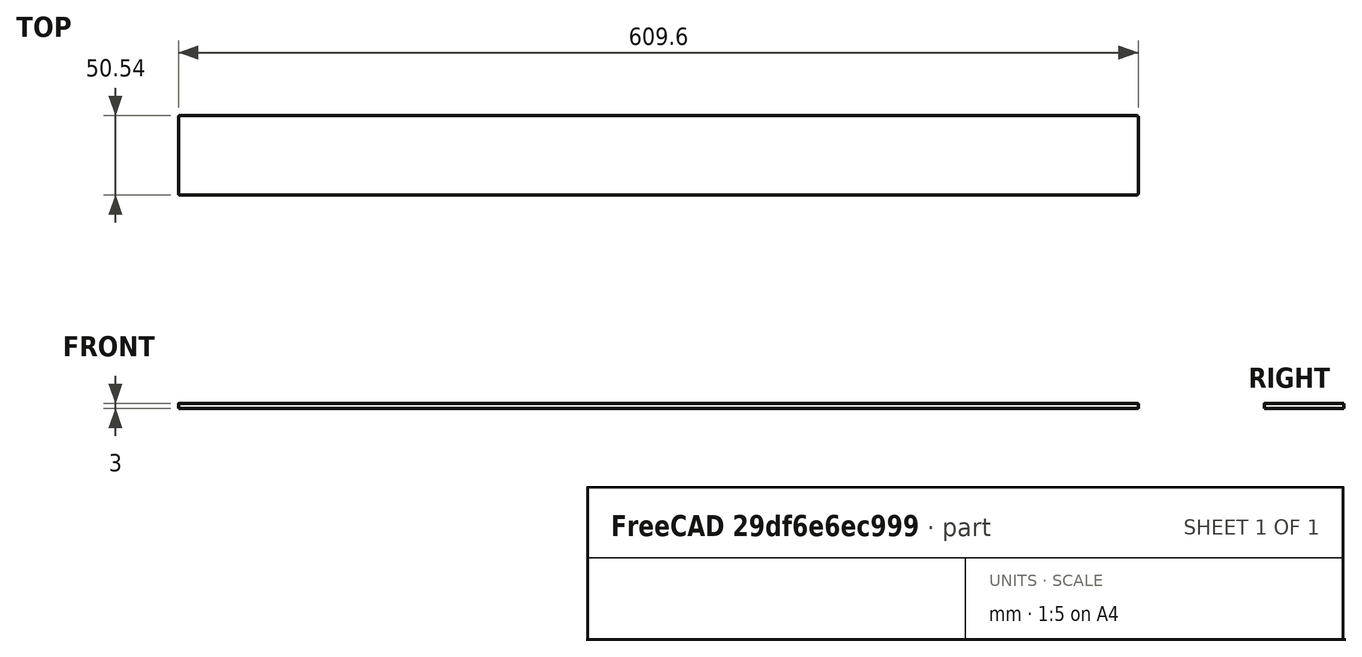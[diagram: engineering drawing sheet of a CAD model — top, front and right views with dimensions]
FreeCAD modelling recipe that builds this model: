
FCSTD DOCUMENT  (FreeCAD 0.20R29603 (Git))
Label: floor_24in
License: All rights reserved
LicenseURL: http://en.wikipedia.org/wiki/All_rights_reserved
objects: Sketcher::SketchObject×1, Spreadsheet::Sheet×1, PartDesign::Pad×1, PartDesign::Body×1
note: 4 computed .brp shape members not serialized (recipe doc carries the construction recipe); baked Part::Feature solids carry a one-line shape summary decoded from their .brp

FEATURE [Sketcher::SketchObject] Sketch
  FullyConstrained = true
  MapMode = 5
  Support = -> [XY_Plane]
  expr: Constraints[19] = Spreadsheet.FilletRadius
  expr: Constraints[20] = Spreadsheet.Width
  expr: Constraints[21] = Spreadsheet.Length
  sketch-geometry (10):
    g0: ArcOfCircle CenterX=-303.8 CenterY=24.275 CenterZ=0 NormalX=0 NormalY=0 NormalZ=1 AngleXU=0 Radius=1 StartAngle=1.5708 EndAngle=3.14159
    g1: LineSegment StartX=-303.8 StartY=25.275 StartZ=0 EndX=303.8 EndY=25.275 EndZ=0
    g2: ArcOfCircle CenterX=303.8 CenterY=24.275 CenterZ=0 NormalX=0 NormalY=0 NormalZ=1 AngleXU=0 Radius=1 StartAngle=1e-15 EndAngle=1.5708
    g3: LineSegment StartX=304.8 StartY=24.275 StartZ=0 EndX=304.8 EndY=-24.275 EndZ=0
    g4: ArcOfCircle CenterX=303.8 CenterY=-24.275 CenterZ=0 NormalX=0 NormalY=0 NormalZ=1 AngleXU=0 Radius=1 StartAngle=4.71239 EndAngle=6.28319
    g5: LineSegment StartX=303.8 StartY=-25.275 StartZ=0 EndX=-303.8 EndY=-25.275 EndZ=0
    g6: ArcOfCircle CenterX=-303.8 CenterY=-24.275 CenterZ=0 NormalX=0 NormalY=0 NormalZ=1 AngleXU=0 Radius=1 StartAngle=3.14159 EndAngle=4.71239
    g7: LineSegment StartX=-304.8 StartY=-24.275 StartZ=0 EndX=-304.8 EndY=24.275 EndZ=0
    g8: GeomPoint X=-304.8 Y=25.275 Z=0
    g9: GeomPoint X=304.8 Y=-25.275 Z=0
  constraints (23):
    c: Tangent(g0,g1) = 1.5708
    c: Tangent(g1,g2) = 1.5708
    c: Tangent(g2,g3) = 1.5708
    c: Tangent(g3,g4) = 1.5708
    c: Tangent(g4,g5) = 1.5708
    c: Tangent(g5,g6) = 1.5708
    c: Tangent(g6,g7) = 1.5708
    c: Tangent(g7,g0) = 1.5708
    c: Horizontal(g1)
    c: Horizontal(g5)
    c: Vertical(g3)
    c: Vertical(g7)
    c: Equal(g0,g2)
    c: Equal(g2,g4)
    c: Equal(g4,g6)
    c: PointOnObject(g8,g1)
    c: PointOnObject(g8,g7)
    c: PointOnObject(g9,g3)
    c: PointOnObject(g9,g5)
    c: Radius(g2) = 1
    c: DistanceY(g4,g1) = 50.55
    c: DistanceX(g0,g2) = 609.6
    c: Symmetric(g8,g9,g-1)
FEATURE [Spreadsheet::Sheet] Spreadsheet
  cells = A2=Parameters; A3=WidthMargin; B3(WidthMargin)==0.25mm; A4=Width; B4(Width)==2in - WidthMargin; A5=Length; B5(Length)==24in; A6=Thickness; B6(Thickness)==3mm; A7=FilletRadius; B7(FilletRadius)==1mm
FEATURE [PartDesign::Pad] Pad
  Direction = (0,0,1)
  Length = 3
  Length2 = 10
  Profile = -> Sketch
  ReferenceAxis = -> Sketch [N_Axis]
  Type = 0
  expr: Length = Spreadsheet.Thickness
FEATURE [PartDesign::Body] Body
  Group = -> [Sketch,Pad]
  Origin = -> Origin
  Tip = -> Pad
